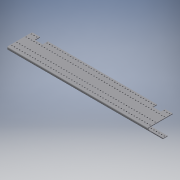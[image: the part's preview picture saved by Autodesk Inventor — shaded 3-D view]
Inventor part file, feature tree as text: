
AUTODESK INVENTOR PART (.ipt)
format: ipt  version: 2016 (Build 200138000, 138)  size: 619,008 bytes
history: native  units: in
note: dims shown in document units (in); Inventor stores cm internally (conversion verified against a paired STEP export)
features: extrude x5, sketch x5, other x1
ambient origin geometry x8: Origin, YZ Plane, XZ Plane, XY Plane, X Axis, Y Axis, Z Axis, Center Point
bodies: Solid1 (feature_tree)
feature tree (11):
  extrude  "Extrusion1"  Depth=0.25in TaperAngle=0.0deg
  extrude  "Extrusion2"  Depth=1.0in TaperAngle=0.0deg
  extrude  "Extrusion3"  [1 undecoded]
  extrude  "Extrusion4"  [1 undecoded]
  extrude  "Extrusion5"  [1 undecoded]
  sketch  "Sketch1"  dims[d0=3.75in d1=0.0in d2=0.25in d3=0.0in]
  sketch  "Sketch2"  dims[d4=1.0in d5=0.0in d7=1.0in d8=0.0in]
  sketch  "Sketch3"  dims[d9=1.0in d10=0.0in]
  sketch  "Sketch4"
  sketch  "Sketch5"
  other  "LPattern2"
note: 3 required parameter values undecoded (feature->parameter linkage not recoverable at this tier; creation-order binding heuristic only, values carry confidence <= 0.55)
